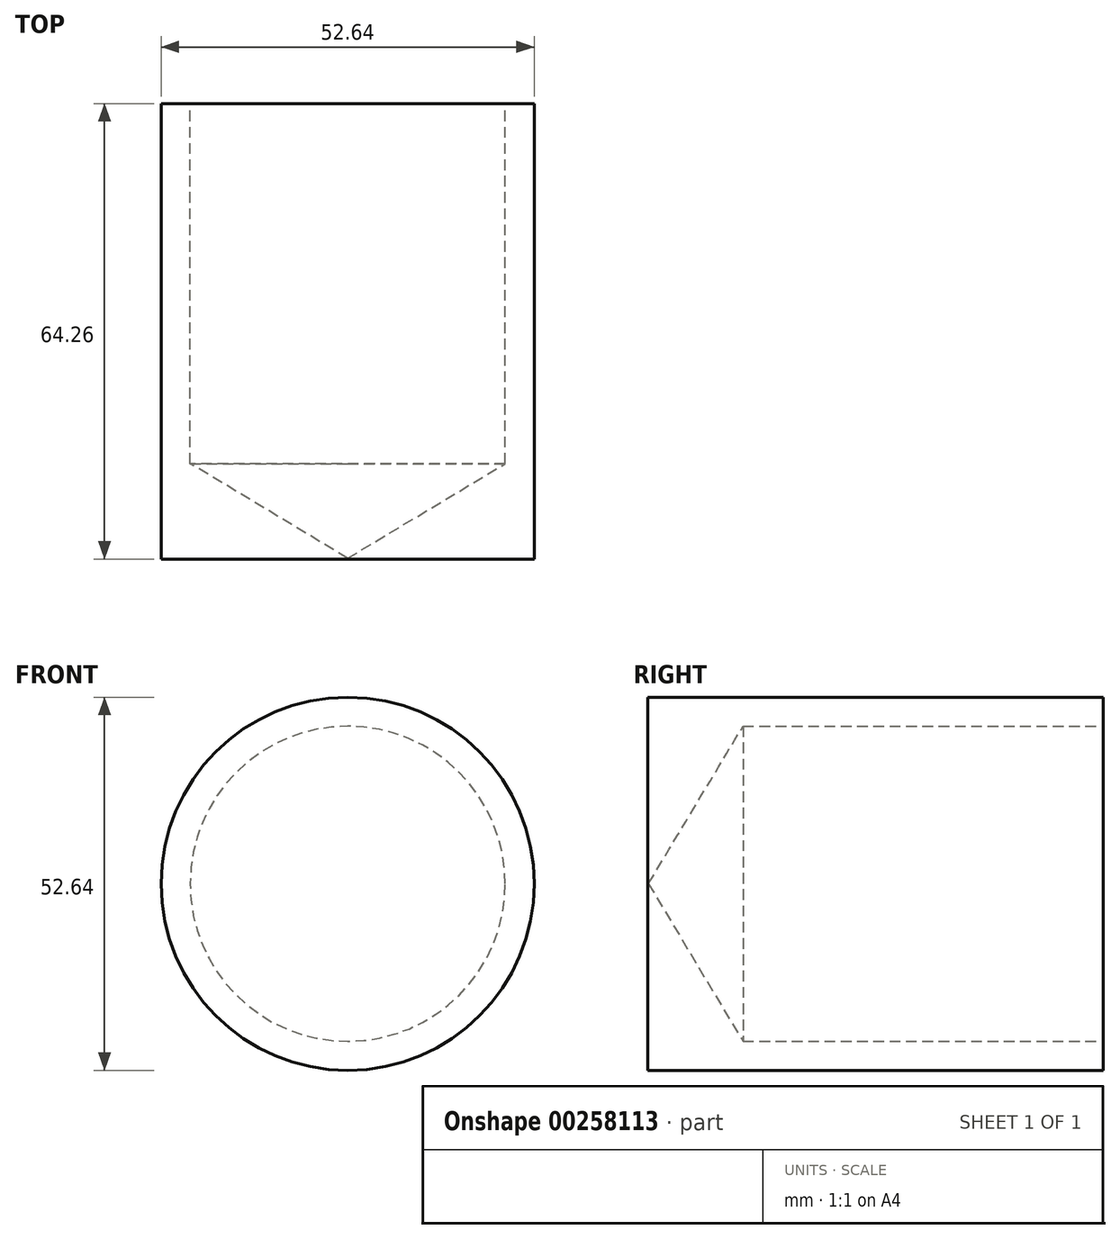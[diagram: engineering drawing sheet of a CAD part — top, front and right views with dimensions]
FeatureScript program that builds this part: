
annotation { "Feature Type Name" : "Feature", "Feature Type Description" : "" }
export const myFeature = defineFeature(function(context is Context, id is Id, definition is map)
    precondition{}
    {
        {
            var Q0;
            Q0=qCreatedBy(makeId("Front.planeOp"),FACE);
            var sketch = newSketch(context, id + "F0", { "sketchPlane" : qUnion([Q0])});
            skCircle(sketch, "E0", {"center": v(0, 0) * mm, "radius": 26.32 * mm});
            skSolve(sketch);
        }
        {
            var Q0;
            Q0=makeQuery(id+"F0.imprint","IMPRINT",FACE,{"disambiguationData":[TD([[makeQuery(id+"F0.imprint","IMPRINT",EDGE,{"derivedFrom":sQuery(id+"F0.wireOp",EDGE,"E0")}),1.0]])]});
            extrude(context, id + "F1", {"entities" : qUnion([Q0]), "depth" : 64.26 * mm});
        }
        {
            var Q0;
            Q0=qCreatedBy(makeId("Front.planeOp"),FACE);
            var sketch = newSketch(context, id + "F2", { "sketchPlane" : qUnion([Q0])});
            skPoint(sketch, "E1", {"position": v(0, 0) * mm});
            skSolve(sketch);
        }
        {
            var Q0;
            Q0=sQuery(id+"F2.wireOp",VERTEX,"E1");
            var Q1;
            Q1=makeQuery(id+"F1.opExtrude","SWEPT_BODY",BODY,{"disambiguationData":[OSD([sQuery(id+"F0.wireOp",EDGE,"E0")])]});
            hole(context, id + "F3", {"style" : HoleStyle.SIMPLE, "endStyle" : HoleEndStyle.BLIND, "oppositeDirection" : true, "holeDiameter" : 44.45 * mm, "holeDepth" : 50.8 * mm, "tappedDepth" : 12.7 * mm, "tapClearance" : 3, "locations" : qUnion([Q0]), "scope" : qUnion([Q1])});
        }
    });
